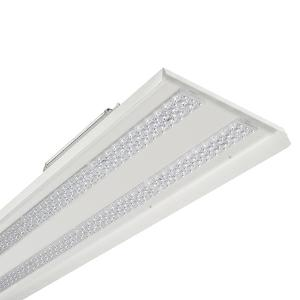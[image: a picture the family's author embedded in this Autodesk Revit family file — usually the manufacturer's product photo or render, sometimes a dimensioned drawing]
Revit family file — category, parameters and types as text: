
# Revit family: 3f_filippi_-_kit_led_retrofit_beta_430_2x_3f_filippi_-_a5309_-_kit_led_beta_430_-_l1551-_2x65w_conc
name_source: partatom
category: Lighting Fixtures
units: mm (PartAtom-declared; Revit-internal decimal feet)

## family parameters
Cut with Voids When Loaded = No
Host = Face
Light Source = No
Part Type = Normal
Room Calculation Point = No
Round Connector Dimension = Use Diameter
Shared = No

## types (1)
- 3F Filippi - Kit LED Retrofit Beta 430 2X (1 x LED, 18071 lm, 120 W, 4000 K)
    Apparent Load = 120 VA
    Approval mark = ENEC
    CIE Flux Codes = 74 92 99 100 100
    Color Rendering = 80
    Color Temperature = 4000 K
    Control Gear = Electronic ballast
    Default Elevation = 1800 mm
    Description = Beta 430 Retrofit Kit to replace the 4x49W T5 Amalgam or the 4x58W T8 version

ILLUMINOTECHNICAL
Luminous efficiency 100% (DLOR 100%, ULOR 0%).
Initial luminous flux of the luminaire 18071 lm.
Symmetric concentrated distribution.
Installation Interdistance Transv.D = 0.60 x hu - Long.D = 1.10 x hu.
Tabular UGR (CIE 117 - 4H-8H; S=0.25H; 70/50/20): RUG 18.7 - 19.1.
Beam angle: 36° - 73°.
Luminous efficacy 151 lm/W.
Lifetime (L93/B10): 30000 h. (tq+25°C)
Lifetime (L90/B10): 50000 h. (tq+25°C)
Lifetime (L85/B10): 80000 h. (tq+25°C)
Lifetime (L80/B10): 100000 h. (tq+25°C)
Lifetime (L85/B10): 50000 h. (tq+40°C)
Sudden decreased luminous flux after 50000 hours: 0% (C0).
Photobiological safety in compliance with IEC/TR 62778: RG0 risk exempt, (IEC 62471).
In compliance with IEC/EN 62722-2-1 - IEC/EN 62717 standards.

SOURCE
2 linear LED modules 65W/840.
Energy efficiency class (UE 2019/2020 - UE 2019/2015): C.
CIE 13.3 Colour rendering index: CRI >80 (R9 <50%).
IES TM-30 Fidelity Index: Rf = 84 Rg = 95.
CCT nominal colour temperature 4000 K.
Colour initial tolerance (MacAdam): SDCM 3.

MECHANICAL
Gear-tray unit hot-galvanised steel, painted in white polyester.
Methacrylate (PMMA) lenses with external flat surface.
Luminaire with limited surface temperature. - D - (EN 60598-2-24)
Dimensions: 1551x430 mm, height 159 mm. Weight 5 kg.
Glow-wire test resistance 850°C.

ELECTRICAL
Halogen Free electronic wiring 230V-50/60Hz, power factor 0.97, THD <25%, constant output current, class I, 2 driver.
Twin-circuit.
Power of the luminaire 120 W.
CE - IEC 60598-1 - EN 60598-1.
SAFE FLICKER: PstLM=<1 and SVM=<0.4 (IEC TR 61547-1 and IEC TR 63158), to ensure a more comfortable and safe light.
Luminaire compliant with EN 60598-2-22 for power supply from a centralised emergency system CPSS (Central Power Supply System), not incorporated in the luminaire - high risk areas excluded. The default power and flux are 100% in AC and 100% in DC.
Ambient temperature from -20°C to +40°C.
Temperature class T6 max 85°C.
Relative humidity UR: <85%.

INSTALLATION
Retrofit.
Correct installation of the retrofit LED kit, compliant with EN 60598-1 and CE marked, inside the 3F Filippi - Beta 4x and 6x i3F 76 Fluorescent luminaires must be only carried out by qualified personnel to ensure compliance with the national installation standards.
Attention: to maintain the degree of protection of the device and for the purposes of validity of the guarantee of the new retrofit kits, it is imperative to replace the old cable guides (on the body of the device) with the new ones supplied.
All accessories dedicated to this product are available on the Catalog and on our website www.3F-Filippi.com.

WARNING
Fixture not suitable for cold stores with an ambient temperature <0°C and/or relative humidity >85%.
Luminaire designed for disposal/recycling at end-of-life.
Replaceable (LED only) light source by a professional. Replaceable control gear by a professional.
    Height = 159 mm
    Lamp = 1 x LED
    Lamp Light Flux = 18071 lm
    Lamp Power = 120 W
    Lamp count = 1
    Length = 1551 mm
    Lifetime = 50000 h
    Luminous efficacy = 151 lm/W
    Manufacturer = 3F Filippi
    ModVariant = No
    Model = 3F Filippi - A5309 - Kit LED Beta 430 - L1551- 2X65W CONC
    Mounting Place = Ceiling
    Mounting Type = Surface mounted
    Number of Poles = 1
    OnlyDefault = Yes
    Power Factor = 1
    Product Name = 3F Filippi - Kit LED Retrofit Beta 430 2X
    Product group = ceiling mounted luminaire
    ProductGroupID = 3
    Protection Class = Protection class I
    Protection Degree = Degree of protection
    RLX_Detail_Level = 1
    RLX_Emergency_Light_Flux = 0 lm
    RLX_Emergency_Type = 0
    RLX_Emergency_Type_DB = No
    RlxData = <blob elided: 69641 chars, md5=5808a78e>
    Socket = socket
    Standby Power = 0 W
    System Light Flux = 18071 lm
    System Power = 120 W
    Type Comments = Product without accessories
    Type Image = 3ffilippi_a5309.jpg
    URL = http://relux.com
    VarID = ---
    Voltage = 0 V
    Weight = 0.00 kg
    Width = 430 mm

## geometry (parser evidence)
native form markers: Blend x4, Sweep x10
no freeform markers — native parametric forms only
